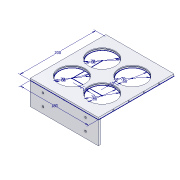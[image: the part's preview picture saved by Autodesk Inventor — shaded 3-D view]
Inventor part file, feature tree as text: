
AUTODESK INVENTOR PART (.ipt)
format: ipt  version: 2020.3 (Build 243373010, 373A)  size: 165,888 bytes
history: native  units: mm
features: sketch x4, extrude x3, hole x2
ambient origin geometry x8: Origin, YZ Plane, XZ Plane, XY Plane, X Axis, Y Axis, Z Axis, Center Point
bodies: Solid1 (feature_tree)
feature tree (9):
  sketch  "Sketch1"  dims[d0=180.0mm d1=200.0mm]
  extrude  "Extrusion1"  Depth=200.0mm
  extrude  "Extrusion2"  Depth=70.0mm
  hole  "Hole1"  [1 undecoded]
  extrude  "Extrusion3"  Depth=5.0mm TaperAngle=0.0deg
  hole  "Hole2"  [1 undecoded]
  sketch  "Sketch2"  dims[d2=70.0mm d3=70.0mm]
  sketch  "Sketch3"  dims[d4=70.0mm d5=70.0mm d6=10.0mm]
  sketch  "Sketch4"  dims[d7=10.0mm d9=5.0mm d10=0.0mm d11=68.0mm d12=68.0mm d13=68.0mm d14=68.0mm d15=3.0mm d16=0.0mm d18=2.0mm d19=2.0mm d20=2.0mm d21=2.0mm d23=40.0mm d24=40.0mm d25=40.0mm d26=40.0mm d28=3.242mm d29=8.0mm d30=3.708mm d31=2.0mm d32=14.3117mm d33=11.8mm d34=0.0mm d35=6.0mm d36=60.0mm d37=0.0mm d38=4.917mm d39=12.0mm d40=3.708mm d41=2.0mm d42=14.3117mm d43=17.1mm d44=0.0mm d45=2.5mm]
note: 2 required parameter values undecoded (feature->parameter linkage not recoverable at this tier; creation-order binding heuristic only, values carry confidence <= 0.55)
